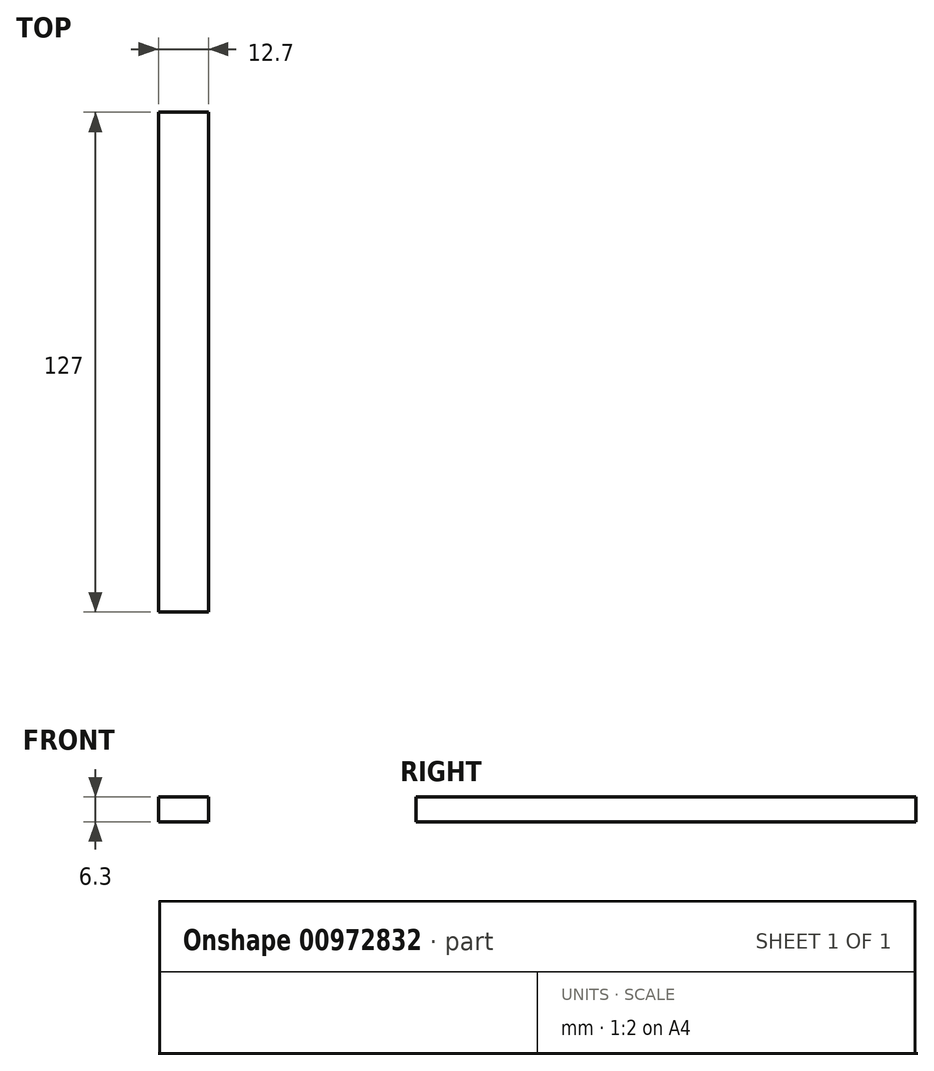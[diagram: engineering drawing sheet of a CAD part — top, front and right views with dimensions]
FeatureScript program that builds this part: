
annotation { "Feature Type Name" : "Feature", "Feature Type Description" : "" }
export const myFeature = defineFeature(function(context is Context, id is Id, definition is map)
    precondition{}
    {
        {
            var Q0;
            Q0=qCreatedBy(makeId("Top.planeOp"),FACE);
            var sketch = newSketch(context, id + "F0", { "sketchPlane" : qUnion([Q0])});
            skLineSegment(sketch, "E0.bottom", {"start": v(6.35, 63.5) * mm, "end": v(-6.35, 63.5) * mm});
            skLineSegment(sketch, "E0.top", {"start": v(6.35, -63.5) * mm, "end": v(-6.35, -63.5) * mm});
            skLineSegment(sketch, "E0.left", {"start": v(6.35, 63.5) * mm, "end": v(6.35, -63.5) * mm});
            skLineSegment(sketch, "E0.right", {"start": v(-6.35, 63.5) * mm, "end": v(-6.35, -63.5) * mm});
            skPoint(sketch, "E0.middle", {"position": v(0, 0) * mm});
            skSolve(sketch);
        }
        {
            var Q0;
            Q0=makeQuery(id+"F0.imprint","IMPRINT",FACE,{"disambiguationData":[TD([[makeQuery(id+"F0.imprint","IMPRINT",EDGE,{"derivedFrom":sQuery(id+"F0.wireOp",EDGE,"E0.bottom")}),1.0]])]});
            extrude(context, id + "F1", {"entities" : qUnion([Q0]), "depth" : 6.3 * mm, "offsetDistance" : 25 * mm});
        }
    });
